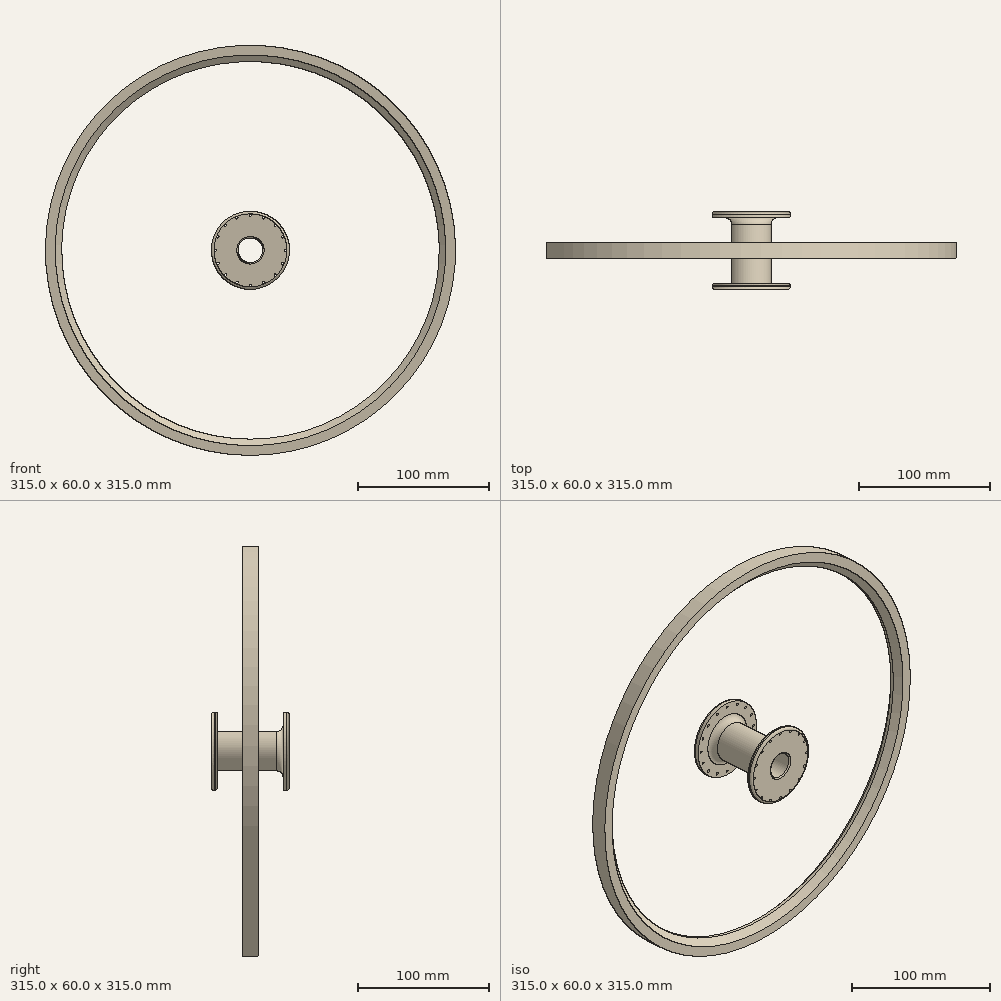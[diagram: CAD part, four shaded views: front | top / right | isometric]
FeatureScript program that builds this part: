
annotation { "Feature Type Name" : "Feature", "Feature Type Description" : "" }
export const myFeature = defineFeature(function(context is Context, id is Id, definition is map)
    precondition{}
    {
        {
            var Q0;
            Q0=qCreatedBy(makeId("Front.planeOp"),FACE);
            var sketch = newSketch(context, id + "F0", { "sketchPlane" : qUnion([Q0])});
            skCircle(sketch, "E0", {"center": v(0, 0) * mm, "radius": 30 * mm});
            skCircle(sketch, "E1", {"center": v(0, 0) * mm, "radius": 9.5 * mm});
            skSolve(sketch);
        }
        {
            var Q0;
            Q0 = qSketchRegion(id + "F0", true);
            extrude(context, id + "F1", {"entities" : qUnion([Q0]), "endBound" : BoundingType.SYMMETRIC, "depth" : 60 * mm});
        }
        {
            var Q0;
            Q0=makeQuery(id+"F1.opExtrude","CAP_FACE",FACE,{"disambiguationData":[OSD([sQuery(id+"F0.wireOp",EDGE,"E0"),sQuery(id+"F0.wireOp",EDGE,"E1")])],"isStart":false});
            var sketch = newSketch(context, id + "F2", { "sketchPlane" : qUnion([Q0])});
            skCircle(sketch, "E2", {"center": v(0, 0) * mm, "radius": 15 * mm});
            skCircle(sketch, "E3", {"center": v(0, 0) * mm, "radius": 30 * mm});
            skSolve(sketch);
        }
        {
            var Q0;
            Q0 = qSketchRegion(id + "F2", true);
            extrude(context, id + "F3", {"entities" : qUnion([Q0]), "operationType" : NewBodyOperationType.REMOVE, "oppositeDirection" : true, "depth" : 55 * mm});
        }
        {
            var Q0;
            Q0=makeQuery(id+"F1.opExtrude","CAP_FACE",FACE,{"disambiguationData":[OSD([sQuery(id+"F0.wireOp",EDGE,"E0"),sQuery(id+"F0.wireOp",EDGE,"E1")])],"isStart":false});
            var sketch = newSketch(context, id + "F4", { "sketchPlane" : qUnion([Q0])});
            skCircle(sketch, "E4", {"center": v(0, 0) * mm, "radius": 30 * mm});
            skCircle(sketch, "E5", {"center": v(0, 0) * mm, "radius": 15 * mm});
            skSolve(sketch);
        }
        {
            var Q0;
            Q0 = qSketchRegion(id + "F4", true);
            extrude(context, id + "F5", {"entities" : qUnion([Q0]), "operationType" : NewBodyOperationType.ADD, "oppositeDirection" : true, "depth" : 5 * mm});
        }
        {
            var Q0;
            Q0=makeQuery(id+"F5.opExtrude","CAP_EDGE",EDGE,{"disambiguationData":[OSD([sQuery(id+"F4.wireOp",EDGE,"E4")])],"isStart":true});
            var Q1;
            Q1=makeQuery(id+"F5.opExtrude","CAP_EDGE",EDGE,{"disambiguationData":[OSD([sQuery(id+"F4.wireOp",EDGE,"E4")])],"isStart":false});
            var Q2;
            Q2=makeQuery(id+"F3.boolean.opBoolean","COPY",EDGE,{"derivedFrom":makeQuery(id+"F3.opExtrude","CAP_EDGE",EDGE,{"disambiguationData":[OSD([sQuery(id+"F2.wireOp",EDGE,"E3")])],"isStart":false})});
            var Q3;
            Q3=makeQuery(id+"F1.opExtrude","CAP_EDGE",EDGE,{"disambiguationData":[OSD([sQuery(id+"F0.wireOp",EDGE,"E0")])],"isStart":true});
            fillet(context, id + "F6", {"entities" : qUnion([Q0, Q1, Q2, Q3]), "radius" : 2 * mm, "tangentPropagation" : true, "allowEdgeOverflow" : false});
        }
        {
            var Q0;
            Q0=makeQuery(id+"F3.boolean.opBoolean","COPY",EDGE,{"derivedFrom":makeQuery(id+"F3.opExtrude","CAP_EDGE",EDGE,{"disambiguationData":[OSD([sQuery(id+"F2.wireOp",EDGE,"E2")])],"isStart":false})});
            var Q1;
            Q1=makeQuery(id+"F5.opExtrude","CAP_EDGE",EDGE,{"disambiguationData":[OSD([sQuery(id+"F4.wireOp",EDGE,"E5")])],"isStart":false});
            fillet(context, id + "F7", {"entities" : qUnion([Q0, Q1]), "radius" : 5 * mm, "tangentPropagation" : true, "allowEdgeOverflow" : false});
        }
        {
            var Q0;
            Q0=makeQuery(id+"F1.opExtrude","CAP_FACE",FACE,{"disambiguationData":[OSD([sQuery(id+"F0.wireOp",EDGE,"E0"),sQuery(id+"F0.wireOp",EDGE,"E1")])],"isStart":true});
            var sketch = newSketch(context, id + "F8", { "sketchPlane" : qUnion([Q0])});
            skLineSegment(sketch, "E6", {"start": v(-4.98, -8.09) * mm, "end": v(0, 0) * mm, "construction": true});
            skCircle(sketch, "E7", {"center": v(0, 0) * mm, "radius": 27 * mm, "construction": true});
            skLineSegment(sketch, "E8", {"start": v(0, 0) * mm, "end": v(0, 27) * mm, "construction": true});
            skCircle(sketch, "E9", {"center": v(0, 27) * mm, "radius": 1 * mm});
            skCircle(sketch, "E10.1.0", {"center": v(-10.33, 24.94) * mm, "radius": 1 * mm});
            skCircle(sketch, "E10.2.0", {"center": v(-19.1, 19.1) * mm, "radius": 1 * mm});
            skCircle(sketch, "E10.3.0", {"center": v(-24.94, 10.33) * mm, "radius": 1 * mm});
            skCircle(sketch, "E10.4.0", {"center": v(-27, 0) * mm, "radius": 1 * mm});
            skCircle(sketch, "E10.5.0", {"center": v(-24.94, -10.33) * mm, "radius": 1 * mm});
            skCircle(sketch, "E10.6.0", {"center": v(-19.1, -19.1) * mm, "radius": 1 * mm});
            skCircle(sketch, "E10.7.0", {"center": v(-10.33, -24.94) * mm, "radius": 1 * mm});
            skCircle(sketch, "E10.8.0", {"center": v(0, -27) * mm, "radius": 1 * mm});
            skCircle(sketch, "E10.9.0", {"center": v(10.33, -24.94) * mm, "radius": 1 * mm});
            skCircle(sketch, "E10.10.0", {"center": v(19.1, -19.1) * mm, "radius": 1 * mm});
            skCircle(sketch, "E10.11.0", {"center": v(24.94, -10.33) * mm, "radius": 1 * mm});
            skCircle(sketch, "E10.12.0", {"center": v(27, 0) * mm, "radius": 1 * mm});
            skCircle(sketch, "E10.13.0", {"center": v(24.94, 10.33) * mm, "radius": 1 * mm});
            skCircle(sketch, "E10.14.0", {"center": v(19.1, 19.1) * mm, "radius": 1 * mm});
            skCircle(sketch, "E10.15.0", {"center": v(10.33, 24.94) * mm, "radius": 1 * mm});
            skSolve(sketch);
        }
        {
            var Q0;
            Q0 = qSketchRegion(id + "F8", true);
            extrude(context, id + "F9", {"entities" : qUnion([Q0]), "operationType" : NewBodyOperationType.REMOVE, "endBound" : BoundingType.THROUGH_ALL, "oppositeDirection" : true, "depth" : 25 * mm});
        }
        {
            var Q0;
            Q0=makeQuery(id+"F1.opExtrude","CAP_EDGE",EDGE,{"disambiguationData":[OSD([sQuery(id+"F0.wireOp",EDGE,"E1")])],"isStart":false});
            var Q1;
            Q1=makeQuery(id+"F1.opExtrude","CAP_EDGE",EDGE,{"disambiguationData":[OSD([sQuery(id+"F0.wireOp",EDGE,"E1")])],"isStart":true});
            fillet(context, id + "F10", {"entities" : qUnion([Q0, Q1]), "radius" : 1 * mm, "tangentPropagation" : true, "allowEdgeOverflow" : false});
        }
        {
            var Q0;
            Q0=qCreatedBy(makeId("Front.planeOp"),FACE);
            var sketch = newSketch(context, id + "F11", { "sketchPlane" : qUnion([Q0])});
            skCircle(sketch, "E11", {"center": v(0, 0) * mm, "radius": 157.5 * mm});
            skCircle(sketch, "E12", {"center": v(0, 0) * mm, "radius": 145 * mm});
            skLineSegment(sketch, "E13", {"start": v(-145, 0) * mm, "end": v(-135, 0) * mm});
            skLineSegment(sketch, "E14.1.0", {"start": v(-142.21, -28.29) * mm, "end": v(-132.4, -26.34) * mm});
            skLineSegment(sketch, "E14.2.0", {"start": v(-133.96, -55.49) * mm, "end": v(-124.72, -51.66) * mm});
            skLineSegment(sketch, "E14.3.0", {"start": v(-120.56, -80.56) * mm, "end": v(-112.25, -75) * mm});
            skLineSegment(sketch, "E14.4.0", {"start": v(-102.53, -102.53) * mm, "end": v(-95.46, -95.46) * mm});
            skLineSegment(sketch, "E14.5.0", {"start": v(-80.56, -120.56) * mm, "end": v(-75, -112.25) * mm});
            skLineSegment(sketch, "E14.6.0", {"start": v(-55.49, -133.96) * mm, "end": v(-51.66, -124.72) * mm});
            skLineSegment(sketch, "E14.7.0", {"start": v(-28.29, -142.21) * mm, "end": v(-26.34, -132.4) * mm});
            skLineSegment(sketch, "E14.8.0", {"start": v(0, -145) * mm, "end": v(0, -135) * mm});
            skLineSegment(sketch, "E14.9.0", {"start": v(28.29, -142.21) * mm, "end": v(26.34, -132.4) * mm});
            skLineSegment(sketch, "E14.10.0", {"start": v(55.49, -133.96) * mm, "end": v(51.66, -124.72) * mm});
            skLineSegment(sketch, "E14.11.0", {"start": v(80.56, -120.56) * mm, "end": v(75, -112.25) * mm});
            skLineSegment(sketch, "E14.12.0", {"start": v(102.53, -102.53) * mm, "end": v(95.46, -95.46) * mm});
            skLineSegment(sketch, "E14.13.0", {"start": v(120.56, -80.56) * mm, "end": v(112.25, -75) * mm});
            skLineSegment(sketch, "E14.14.0", {"start": v(133.96, -55.49) * mm, "end": v(124.72, -51.66) * mm});
            skLineSegment(sketch, "E14.15.0", {"start": v(142.21, -28.29) * mm, "end": v(132.4, -26.34) * mm});
            skLineSegment(sketch, "E14.16.0", {"start": v(145, 0) * mm, "end": v(135, 0) * mm});
            skLineSegment(sketch, "E14.17.0", {"start": v(142.21, 28.29) * mm, "end": v(132.4, 26.34) * mm});
            skLineSegment(sketch, "E14.18.0", {"start": v(133.96, 55.49) * mm, "end": v(124.72, 51.66) * mm});
            skLineSegment(sketch, "E14.19.0", {"start": v(120.56, 80.56) * mm, "end": v(112.25, 75) * mm});
            skLineSegment(sketch, "E14.20.0", {"start": v(102.53, 102.53) * mm, "end": v(95.46, 95.46) * mm});
            skLineSegment(sketch, "E14.21.0", {"start": v(80.56, 120.56) * mm, "end": v(75, 112.25) * mm});
            skLineSegment(sketch, "E14.22.0", {"start": v(55.49, 133.96) * mm, "end": v(51.66, 124.72) * mm});
            skLineSegment(sketch, "E14.23.0", {"start": v(28.29, 142.21) * mm, "end": v(26.34, 132.4) * mm});
            skLineSegment(sketch, "E14.24.0", {"start": v(0, 145) * mm, "end": v(0, 135) * mm});
            skLineSegment(sketch, "E14.25.0", {"start": v(-28.29, 142.21) * mm, "end": v(-26.34, 132.4) * mm});
            skLineSegment(sketch, "E14.26.0", {"start": v(-55.49, 133.96) * mm, "end": v(-51.66, 124.72) * mm});
            skLineSegment(sketch, "E14.27.0", {"start": v(-80.56, 120.56) * mm, "end": v(-75, 112.25) * mm});
            skLineSegment(sketch, "E14.28.0", {"start": v(-102.53, 102.53) * mm, "end": v(-95.46, 95.46) * mm});
            skLineSegment(sketch, "E14.29.0", {"start": v(-120.56, 80.56) * mm, "end": v(-112.25, 75) * mm});
            skLineSegment(sketch, "E14.30.0", {"start": v(-133.96, 55.49) * mm, "end": v(-124.72, 51.66) * mm});
            skLineSegment(sketch, "E14.31.0", {"start": v(-142.21, 28.29) * mm, "end": v(-132.4, 26.34) * mm});
            skSolve(sketch);
        }
        {
            var Q0;
            Q0 = qSketchRegion(id + "F11", true);
            extrude(context, id + "F12", {"entities" : qUnion([Q0]), "operationType" : NewBodyOperationType.ADD, "endBound" : BoundingType.SYMMETRIC, "depth" : 12.5 * mm});
        }
        {
            var Q0;
            Q0=makeQuery(id+"F12.opExtrude","CAP_EDGE",EDGE,{"disambiguationData":[OSD([sQuery(id+"F11.wireOp",EDGE,"E12")])],"isStart":false});
            chamfer(context, id + "F13", {"entities" : qUnion([Q0]), "width" : 5 * mm, "tangentPropagation" : true});
        }
        {
            var Q0;
            Q0=makeQuery(id+"F12.opExtrude","CAP_EDGE",EDGE,{"disambiguationData":[OSD([sQuery(id+"F11.wireOp",EDGE,"E12")])],"isStart":true});
            chamfer(context, id + "F14", {"entities" : qUnion([Q0]), "width" : 5 * mm, "tangentPropagation" : true});
        }
    });
